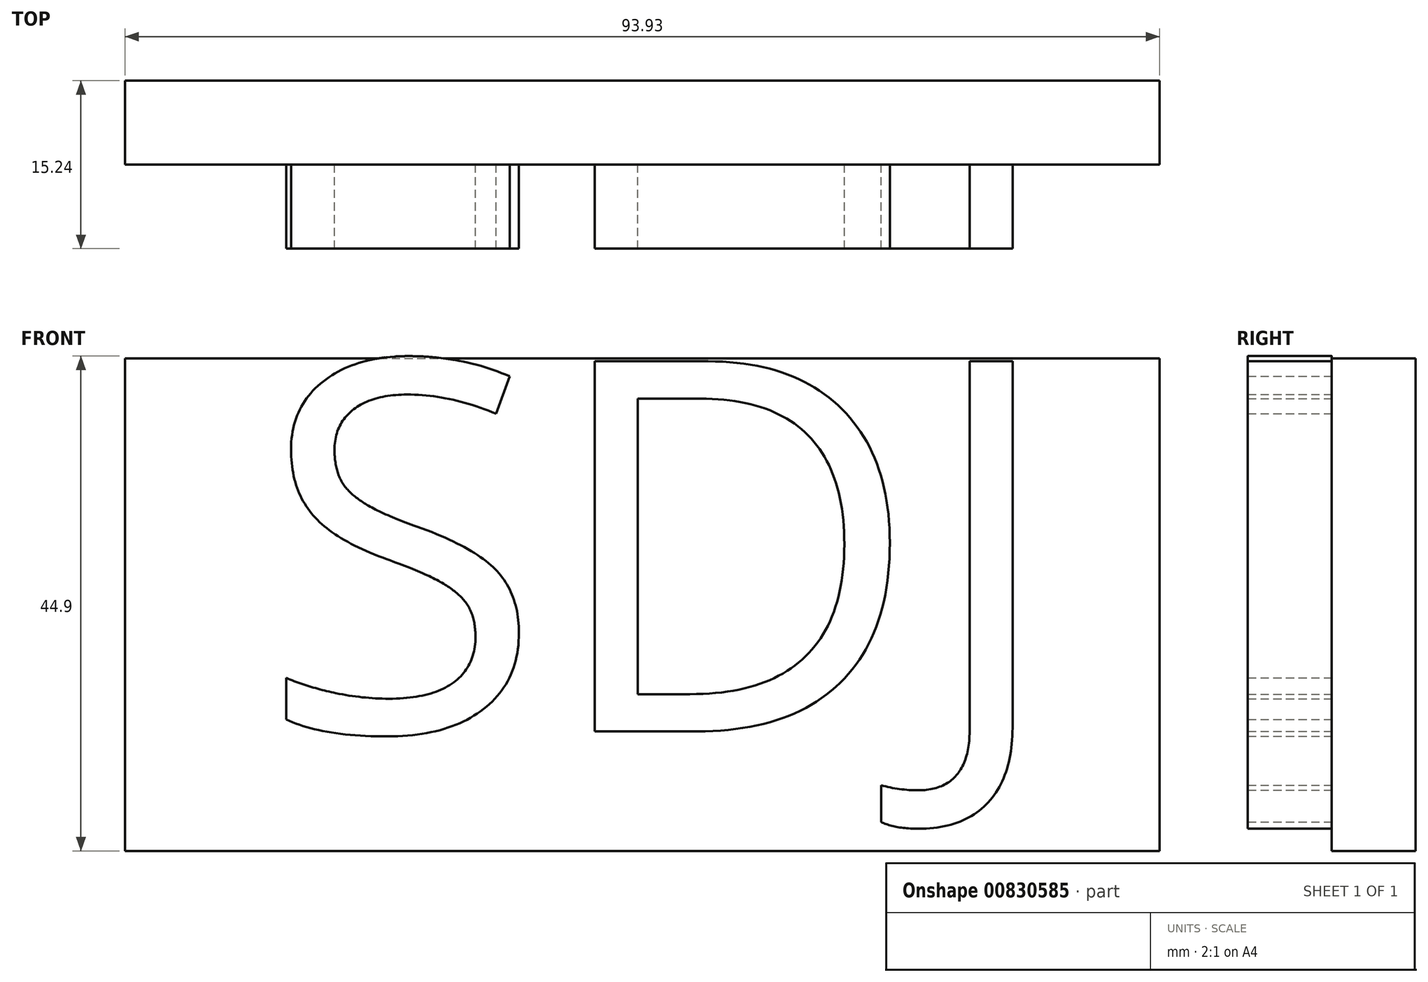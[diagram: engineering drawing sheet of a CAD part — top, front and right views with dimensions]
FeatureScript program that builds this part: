
annotation { "Feature Type Name" : "Feature", "Feature Type Description" : "" }
export const myFeature = defineFeature(function(context is Context, id is Id, definition is map)
    precondition{}
    {
        {
            var Q0;
            Q0=qCreatedBy(makeId("Front.planeOp"),FACE);
            var sketch = newSketch(context, id + "F0", { "sketchPlane" : qUnion([Q0])});
            skLineSegment(sketch, "E0.bottom", {"start": v(0, 0) * mm, "end": v(93.93, 0) * mm});
            skLineSegment(sketch, "E0.top", {"start": v(0, 44.7) * mm, "end": v(93.93, 44.7) * mm});
            skLineSegment(sketch, "E0.left", {"start": v(0, 0) * mm, "end": v(0, 44.7) * mm});
            skLineSegment(sketch, "E0.right", {"start": v(93.93, 0) * mm, "end": v(93.93, 44.7) * mm});
            skSolve(sketch);
        }
        {
            var Q0;
            Q0=makeQuery(id+"F0.imprint","IMPRINT",FACE,{"disambiguationData":[TD([[makeQuery(id+"F0.imprint","IMPRINT",EDGE,{"derivedFrom":sQuery(id+"F0.wireOp",EDGE,"E0.bottom")}),1.0]])]});
            extrude(context, id + "F1", {"entities" : qUnion([Q0]), "depth" : 7.62 * mm, "offsetDistance" : 25.4 * mm});
        }
        {
            var Q0;
            Q0=makeQuery(id+"F1.opExtrude","CAP_FACE",FACE,{"disambiguationData":[OSD([sQuery(id+"F0.wireOp",EDGE,"E0.bottom"),sQuery(id+"F0.wireOp",EDGE,"E0.top"),sQuery(id+"F0.wireOp",EDGE,"E0.left"),sQuery(id+"F0.wireOp",EDGE,"E0.right")])],"isStart":false});
            var sketch = newSketch(context, id + "F2", { "sketchPlane" : qUnion([Q0])});
            skText(sketch, "E1", { "text": "SDJ", "fontName": "OpenSans-Regular.ttf"});
            const initialGuessF2  = {"E1": [0.0122, 0.01085, 1, 0, 0.03386]};
            skSetInitialGuess(sketch, initialGuessF2);
            skSolve(sketch);
        }
        {
            var Q0;
            Q0 = qSketchRegion(id + "F2", true);
            extrude(context, id + "F3", {"entities" : qUnion([Q0]), "operationType" : NewBodyOperationType.ADD, "depth" : 7.62 * mm, "offsetDistance" : 25.4 * mm});
        }
    });
